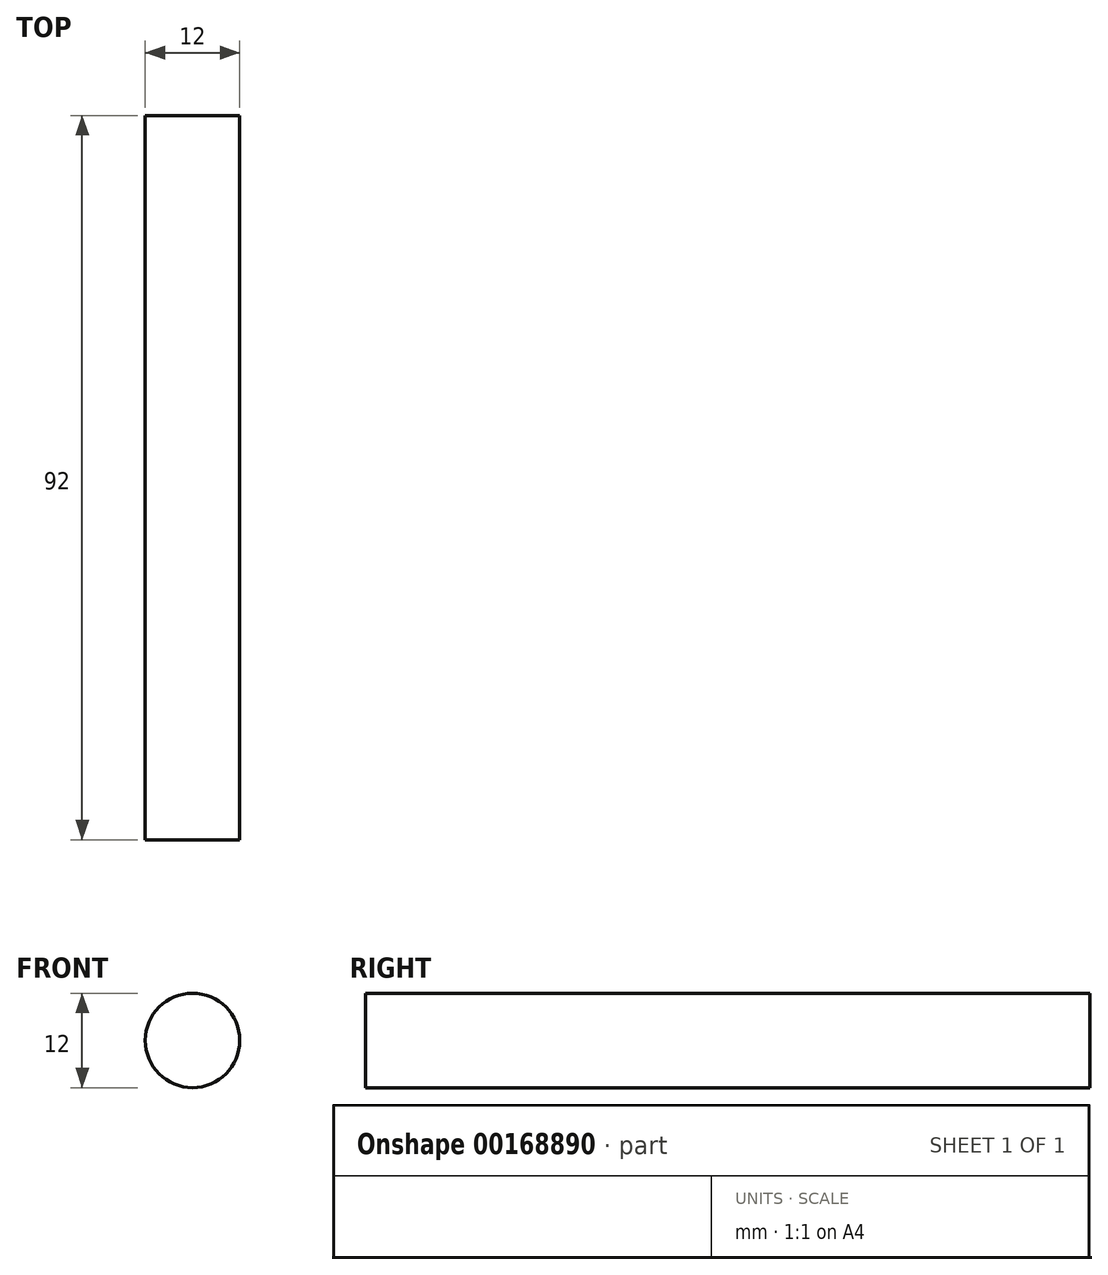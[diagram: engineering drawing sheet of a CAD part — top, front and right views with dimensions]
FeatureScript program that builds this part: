
annotation { "Feature Type Name" : "Feature", "Feature Type Description" : "" }
export const myFeature = defineFeature(function(context is Context, id is Id, definition is map)
    precondition{}
    {
        {
            var Q0;
            Q0=qCreatedBy(makeId("Front.planeOp"),FACE);
            var sketch = newSketch(context, id + "F0", { "sketchPlane" : qUnion([Q0])});
            skCircle(sketch, "E0", {"center": v(0, 0) * mm, "radius": 6 * mm});
            skSolve(sketch);
        }
        {
            var Q0;
            Q0 = qSketchRegion(id + "F0", true);
            extrude(context, id + "F1", {"entities" : qUnion([Q0]), "depth" : 92 * mm});
        }
    });
